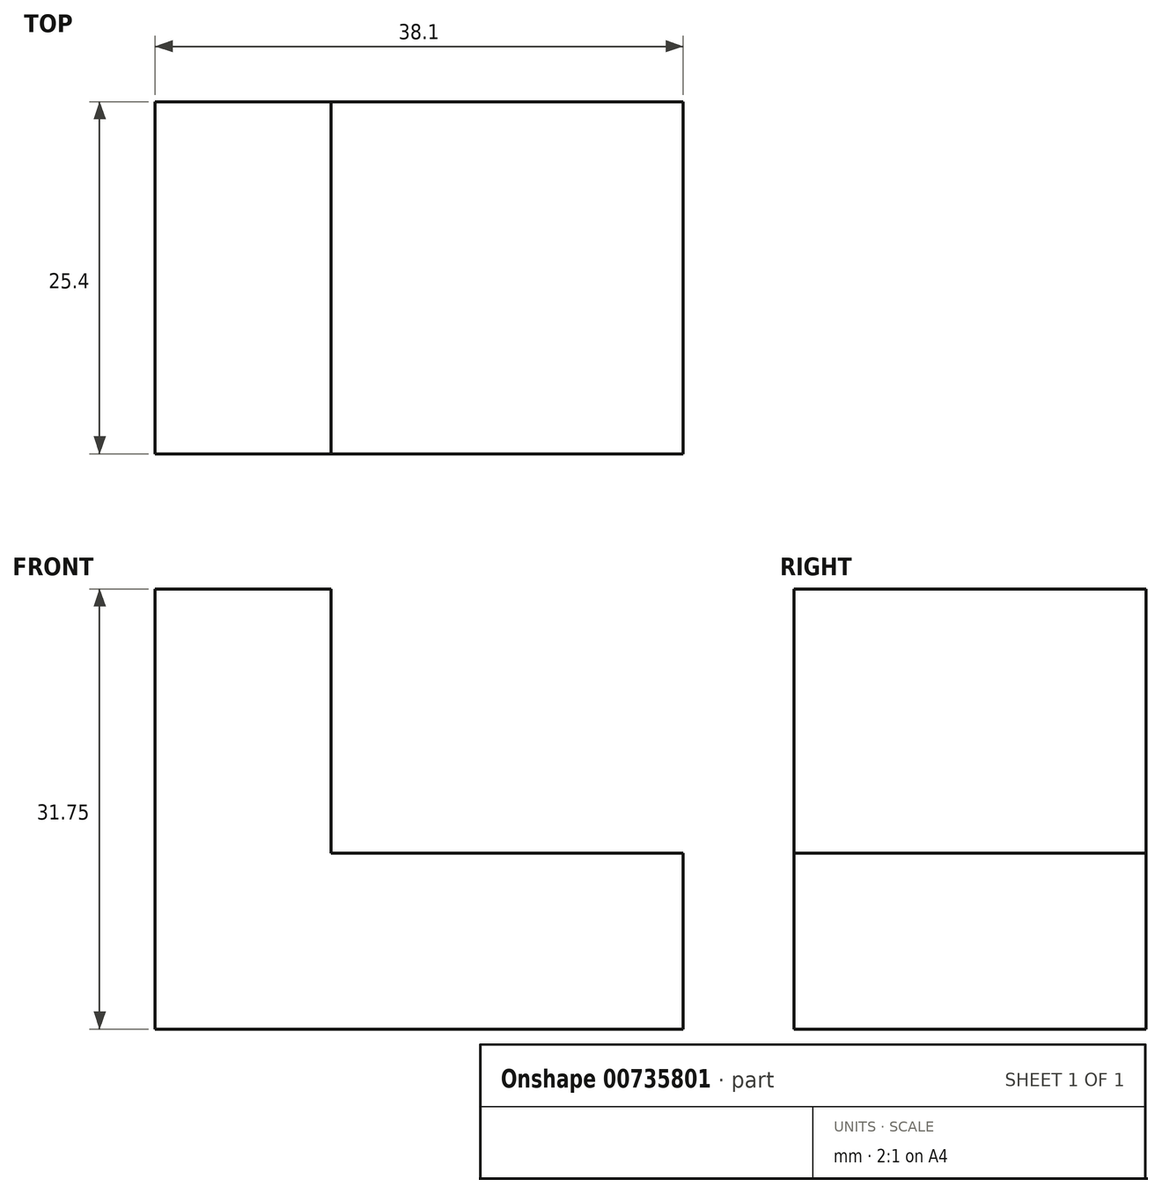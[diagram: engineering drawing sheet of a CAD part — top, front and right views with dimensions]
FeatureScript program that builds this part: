
annotation { "Feature Type Name" : "Feature", "Feature Type Description" : "" }
export const myFeature = defineFeature(function(context is Context, id is Id, definition is map)
    precondition{}
    {
        {
            var Q0;
            Q0=qCreatedBy(makeId("Front.planeOp"),FACE);
            var sketch = newSketch(context, id + "F0", { "sketchPlane" : qUnion([Q0])});
            skLineSegment(sketch, "E0", {"start": v(0, 0) * mm, "end": v(38.1, 0) * mm});
            skLineSegment(sketch, "E1", {"start": v(38.1, 0) * mm, "end": v(38.1, 12.7) * mm});
            skLineSegment(sketch, "E2", {"start": v(38.1, 12.7) * mm, "end": v(12.7, 12.7) * mm});
            skLineSegment(sketch, "E3", {"start": v(12.7, 12.7) * mm, "end": v(12.7, 31.75) * mm});
            skLineSegment(sketch, "E4", {"start": v(12.7, 31.75) * mm, "end": v(0, 31.75) * mm});
            skLineSegment(sketch, "E5", {"start": v(0, 31.75) * mm, "end": v(0, 0) * mm});
            skSolve(sketch);
        }
        {
            var Q0;
            Q0=makeQuery(id+"F0.imprint","IMPRINT",FACE,{"disambiguationData":[TD([[makeQuery(id+"F0.imprint","IMPRINT",EDGE,{"derivedFrom":sQuery(id+"F0.wireOp",EDGE,"E0")}),1.0]])]});
            extrude(context, id + "F1", {"entities" : qUnion([Q0]), "depth" : 25.4 * mm, "offsetDistance" : 25.4 * mm});
        }
    });
